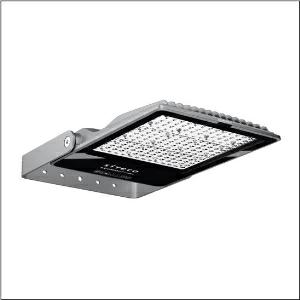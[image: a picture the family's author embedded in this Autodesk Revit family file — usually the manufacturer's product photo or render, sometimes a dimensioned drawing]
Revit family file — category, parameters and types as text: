
# Revit family: sicompact_r__31_midi___pl32_5xa7581d1k23_6975
name_source: partatom
category: Lighting Fixtures
units: mm (PartAtom-declared; Revit-internal decimal feet)

## family parameters
Cut with Voids When Loaded = No
Host = Face
Light Source = No
Part Type = Normal
Room Calculation Point = No
Round Connector Dimension = Use Diameter
Shared = No

## types (1)
- SiCompact® 31 midi  PL32 (1 x LED, 27000 lm, 171 W, 3000K)
    Apparent Load = 171 VA
    CIE Flux Codes = 32 69 98 100 100
    Color Rendering = 70
    Color Temperature = 3000K
    Default Elevation = 1800 mm
    Description = SiCompact® 31 midi, floodlight, primary light control with lens, of plastic, of toughened safety glass, transparent, light distribution: PL32, light emission: direct distribution, primary light characteristic: asymmetric, installation type: surface-mounted, LED, High Power LED, rated luminous flux: 27.000lm, luminous efficacy: 158lm/W, light colour: 730, colour temperature: 3000K, control gear: ECG, with cable, 3x 1.5mm², mains connection: 220..240V, AC, 50/60Hz, connection cable pre-assembled, cable length: 2m, rated input power: 171W, of diecast aluminium, specular, metallic grey (RAL 9006), length: 560mm, width: 330mm, height: 62mm, bracket, of sheet steel, coated, metallic grey (RAL 9006), ON/OFF, protection rating (complete): IP66, insulation class (complete): insulation class I (protective earthing), certification: CE, ENEC, impact resistance: IK08, permissible operating ambient temperature: -40..+45°C, packaging unit: 1 piece

Light Distribution: PL32
    Height = 62 mm  [stored 0.203412 ft]
    Lamp = 1 x LED
    Lamp Light Flux = 27000 lm
    Lamp Power = 171 W
    Lamp count = 1
    Length = 560 mm
    Luminous efficacy = 158 lm/W
    Manufacturer = Siteco
    ModVariant = No
    Model = 5XA7581D1K23
    Mounting Place = Wall
    Mounting Type = Surface mounted
    Number of Poles = 1
    OnlyDefault = Yes
    Power Factor = 1
    Product Name = SiCompact® 31 midi | PL32
    Product group = floodlight | wall mounted
    ProductGroupID = 2001
    Protection Class = Protection class I
    Protection Degree = IP 66
    RLX_Detail_Level = 1
    RLX_Emergency_Light_Flux = 0 lm
    RLX_Emergency_Type = 0
    RLX_Emergency_Type_DB = No
    RlxData = <blob elided: 98305 chars, md5=2c40ee54>
    Socket = socket
    Standby Power = 0 W
    System Light Flux = 27000 lm
    System Power = 171 W
    Type Comments = Product without accessories
    Type Image = l_1006415.jpg
    URL = http://relux.com
    VarID = ---
    Voltage = 0 V
    Weight = 0.00 kg
    Width = 333 mm

note: [stored X ft] marks values corroborated as IEEE doubles in the binary element streams (Revit-internal decimal feet)

## geometry (parser evidence)
native form markers: Blend x4, Sweep x12
no freeform markers — native parametric forms only
